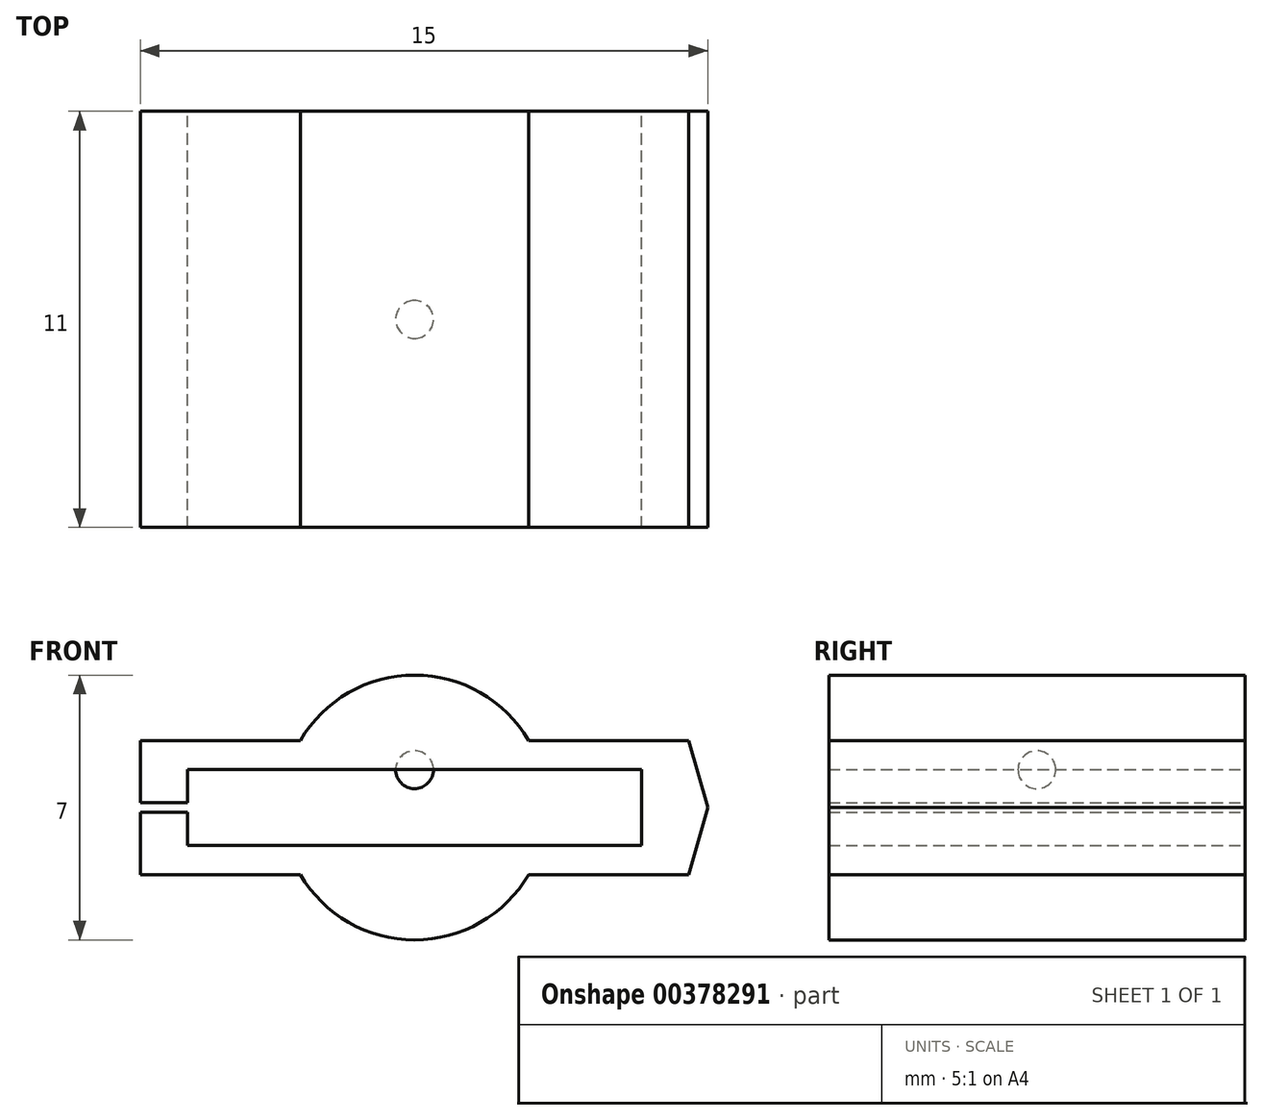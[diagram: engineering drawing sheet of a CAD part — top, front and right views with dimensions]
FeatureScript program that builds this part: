
annotation { "Feature Type Name" : "Feature", "Feature Type Description" : "" }
export const myFeature = defineFeature(function(context is Context, id is Id, definition is map)
    precondition{}
    {
        {
            var Q0;
            Q0=qCreatedBy(makeId("Front.planeOp"),FACE);
            var sketch = newSketch(context, id + "F0", { "sketchPlane" : qUnion([Q0])});
            skLineSegment(sketch, "E0.bottom", {"start": v(7.25, 1.77) * mm, "end": v(3.02, 1.77) * mm});
            skLineSegment(sketch, "E0.top", {"start": v(7.25, -1.77) * mm, "end": v(3.02, -1.77) * mm});
            skLineSegment(sketch, "E0.right", {"start": v(-7.25, 1.77) * mm, "end": v(-7.25, 0.12) * mm});
            skPoint(sketch, "E0.middle", {"position": v(0, 0) * mm});
            skArc(sketch, "E1", {"start": v(3.02, 1.77) * mm, "mid": v(0, 3.5) * mm, "end": v(-3.02, 1.77) * mm});
            skLineSegment(sketch, "E2.bottom", {"start": v(6, 1) * mm, "end": v(0, 1) * mm});
            skLineSegment(sketch, "E2.top", {"start": v(6, -1) * mm, "end": v(0, -1) * mm});
            skLineSegment(sketch, "E2.right", {"start": v(-7.25, 1) * mm, "end": v(-7.25, 0.12) * mm});
            skPoint(sketch, "E3", {"position": v(-3.02, -1.77) * mm});
            skPoint(sketch, "E4", {"position": v(3.02, -1.77) * mm});
            skPoint(sketch, "E5", {"position": v(3.02, 1.77) * mm});
            skPoint(sketch, "E6", {"position": v(-3.02, 1.77) * mm});
            skLineSegment(sketch, "E7.bottom", {"start": v(-7.25, 0.12) * mm, "end": v(-6, 0.12) * mm});
            skLineSegment(sketch, "E7.top", {"start": v(-7.25, -0.13) * mm, "end": v(-6, -0.13) * mm});
            skPoint(sketch, "E7.middle", {"position": v(-5.37, 0) * mm});
            skArc(sketch, "E8.trimOffspring", {"start": v(-3.35, 1) * mm, "mid": v(-3.5, 0) * mm, "end": v(-3.35, -1) * mm, "construction": true});
            skLineSegment(sketch, "E9.trimOffspring", {"start": v(-3.02, 1.77) * mm, "end": v(-7.25, 1.77) * mm});
            skArc(sketch, "E10.trimOffspring", {"start": v(3.35, -1) * mm, "mid": v(3.5, 0) * mm, "end": v(3.35, 1) * mm, "construction": true});
            skLineSegment(sketch, "E11.trimOffspring", {"start": v(-3.02, -1.77) * mm, "end": v(-7.25, -1.77) * mm});
            skArc(sketch, "E12.trimOffspring", {"start": v(-3.02, -1.77) * mm, "mid": v(0, -3.5) * mm, "end": v(3.02, -1.77) * mm});
            skPoint(sketch, "E13.orphan", {"position": v(-3.5, 0) * mm});
            skPoint(sketch, "E14.start.orphan", {"position": v(-7.25, 0) * mm});
            skLineSegment(sketch, "E15.trimOffspring", {"start": v(-7.25, -0.13) * mm, "end": v(-7.25, -1.77) * mm});
            skPoint(sketch, "E16.trimOffspring.end.orphan", {"position": v(-7.25, -1) * mm});
            skPoint(sketch, "E17.orphan", {"position": v(-3.5, 0.12) * mm});
            skPoint(sketch, "E18.orphan", {"position": v(-3.5, -0.13) * mm});
            skLineSegment(sketch, "E19", {"start": v(7.25, 1.77) * mm, "end": v(7.75, 0) * mm});
            skLineSegment(sketch, "E20", {"start": v(7.25, -1.77) * mm, "end": v(7.75, 0) * mm});
            skPoint(sketch, "E21.orphan", {"position": v(7.25, 1) * mm});
            skPoint(sketch, "E2.left.end.orphan", {"position": v(7.25, -1) * mm});
            skPoint(sketch, "E2.left.start.orphan", {"position": v(7.25, 0) * mm});
            skLineSegment(sketch, "E22", {"start": v(7.25, 1.77) * mm, "end": v(7.25, -1.77) * mm, "construction": true});
            skPoint(sketch, "E23", {"position": v(0, 1) * mm});
            skPoint(sketch, "E24", {"position": v(0, -1) * mm});
            skLineSegment(sketch, "E25", {"start": v(0, 2.12) * mm, "end": v(0, -2.1) * mm, "construction": true});
            skLineSegment(sketch, "E26", {"start": v(0, 1) * mm, "end": v(-6, 1) * mm});
            skLineSegment(sketch, "E27", {"start": v(0, -1) * mm, "end": v(-6, -1) * mm});
            skLineSegment(sketch, "E28", {"start": v(-6, 1) * mm, "end": v(-6, 0.12) * mm});
            skLineSegment(sketch, "E29", {"start": v(-6, -1) * mm, "end": v(-6, -0.13) * mm});
            skLineSegment(sketch, "E30", {"start": v(-6, -0.13) * mm, "end": v(-3.5, -0.13) * mm, "construction": true});
            skLineSegment(sketch, "E31", {"start": v(-6, 0.12) * mm, "end": v(-3.5, 0.12) * mm, "construction": true});
            skLineSegment(sketch, "E32", {"start": v(6, 1) * mm, "end": v(6, -1) * mm});
            skLineSegment(sketch, "E33", {"start": v(0, 3.5) * mm, "end": v(6.76, 3.5) * mm});
            skSolve(sketch);
        }
        {
            var Q0;
            Q0=makeQuery(id+"F0.imprint","IMPRINT",FACE,{"disambiguationData":[TD([[makeQuery(id+"F0.imprint","IMPRINT",EDGE,{"derivedFrom":sQuery(id+"F0.wireOp",EDGE,"E0.bottom")}),1.0]])]});
            extrude(context, id + "F1", {"entities" : qUnion([Q0]), "offsetDistance" : 25 * mm, "depth" : 11 * mm});
        }
        {
            var Q0;
            Q0=makeQuery(id+"F1.opExtrude","SWEPT_FACE",FACE,{"disambiguationData":[OSD([sQuery(id+"F0.wireOp",EDGE,"E2.bottom")])]});
            var sketch = newSketch(context, id + "F2", { "sketchPlane" : qUnion([Q0])});
            skLineSegment(sketch, "E34", {"start": v(0, 0) * mm, "end": v(0, 6) * mm});
            skLineSegment(sketch, "E35", {"start": v(3.45, 5.5) * mm, "end": v(0, 5.5) * mm});
            skPoint(sketch, "E35.startSnap0", {"position": v(6, 5.5) * mm});
            skPoint(sketch, "E36", {"position": v(0, 5.5) * mm});
            skCircle(sketch, "E37", {"center": v(0, 5.5) * mm, "radius": 0.5 * mm});
            skSolve(sketch);
        }
        {
            var Q0;
            {var subQ0=sQuery(id+"F2.wireOp",EDGE,"E34");var subQ1=makeQuery(id+"F2.imprint","INTERSECT",VERTEX,{"derivedFrom":[subQ0,sQuery(id+"F2.wireOp",EDGE,"E35")]});Q0=makeQuery(id+"F2.imprint","IMPRINT",FACE,{"disambiguationData":[TD([[makeQuery(id+"F2.imprint","IMPRINT",EDGE,{"disambiguationData":[TD([[subQ1,1.0]])],"derivedFrom":subQ0}),1.0]])]});}
            var Q1;
            Q1=sQuery(id+"F2.wireOp",EDGE,"E34");
            revolve(context, id + "F3", {"entities" : qUnion([Q0]), "axis" : qUnion([Q1]), "revolveType" : RevolveType.FULL});
        }
    });
